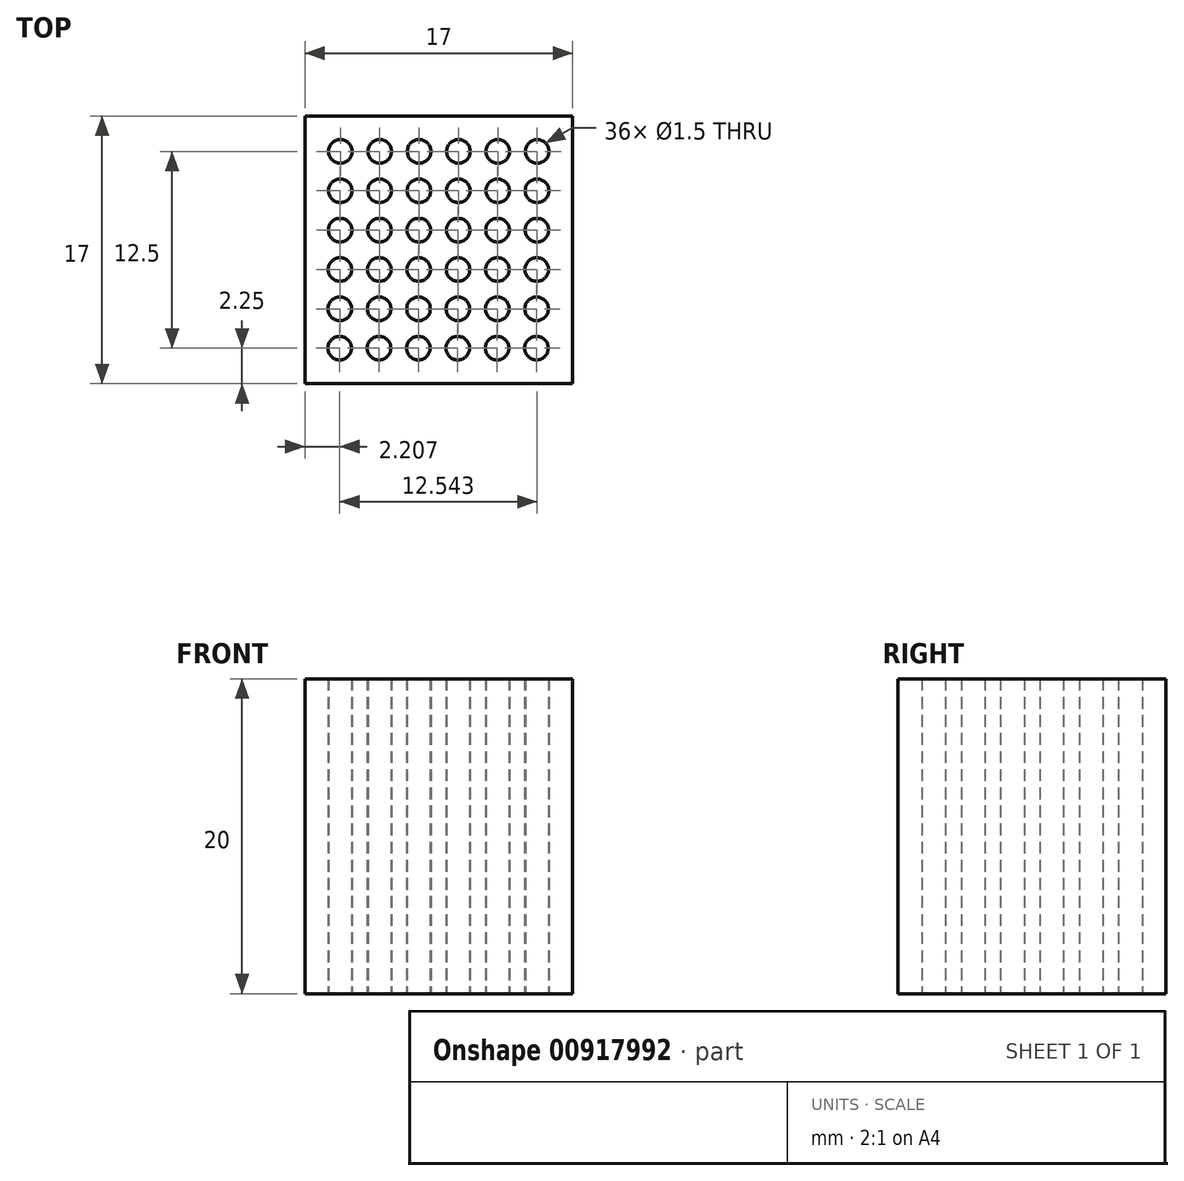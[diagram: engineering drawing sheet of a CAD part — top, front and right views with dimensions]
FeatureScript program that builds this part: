
annotation { "Feature Type Name" : "Feature", "Feature Type Description" : "" }
export const myFeature = defineFeature(function(context is Context, id is Id, definition is map)
    precondition{}
    {
        {
            var Q0;
            Q0=qCreatedBy(makeId("Top.planeOp"),FACE);
            var sketch = newSketch(context, id + "F0", { "sketchPlane" : qUnion([Q0])});
            skLineSegment(sketch, "E0.bottom", {"start": v(-8.5, 8.5) * mm, "end": v(8.5, 8.5) * mm});
            skLineSegment(sketch, "E0.top", {"start": v(-8.5, -8.5) * mm, "end": v(8.5, -8.5) * mm});
            skLineSegment(sketch, "E0.left", {"start": v(-8.5, 8.5) * mm, "end": v(-8.5, -8.5) * mm});
            skLineSegment(sketch, "E0.right", {"start": v(8.5, 8.5) * mm, "end": v(8.5, -8.5) * mm});
            skPoint(sketch, "E0.middle", {"position": v(0, 0) * mm});
            skLineSegment(sketch, "E1", {"start": v(-8.5, 8.5) * mm, "end": v(-6.25, 8.5) * mm});
            skLineSegment(sketch, "E2", {"start": v(-6.25, 8.5) * mm, "end": v(-3.75, 8.5) * mm});
            skLineSegment(sketch, "E3", {"start": v(-3.75, 8.5) * mm, "end": v(-1.25, 8.5) * mm});
            skLineSegment(sketch, "E4", {"start": v(-1.25, 8.5) * mm, "end": v(1.25, 8.5) * mm});
            skLineSegment(sketch, "E5", {"start": v(1.25, 8.5) * mm, "end": v(3.75, 8.5) * mm});
            skLineSegment(sketch, "E6", {"start": v(3.75, 8.5) * mm, "end": v(6.25, 8.5) * mm});
            skLineSegment(sketch, "E7", {"start": v(6.25, 8.5) * mm, "end": v(8.5, 8.5) * mm});
            skLineSegment(sketch, "E8", {"start": v(-8.5, 8.5) * mm, "end": v(-8.5, 6.25) * mm});
            skLineSegment(sketch, "E9", {"start": v(-8.5, 6.25) * mm, "end": v(-8.5, 3.75) * mm});
            skLineSegment(sketch, "E10", {"start": v(-8.5, 1.25) * mm, "end": v(-8.5, -1.25) * mm});
            skLineSegment(sketch, "E11", {"start": v(-8.5, -1.25) * mm, "end": v(-8.5, -3.75) * mm});
            skLineSegment(sketch, "E12", {"start": v(-8.5, -3.75) * mm, "end": v(-8.5, -6.25) * mm});
            skLineSegment(sketch, "E13", {"start": v(-8.5, -6.25) * mm, "end": v(-8.5, -8.5) * mm});
            skLineSegment(sketch, "E14", {"start": v(-8.5, 3.75) * mm, "end": v(-8.5, 1.25) * mm});
            skCircle(sketch, "E15", {"center": v(-6.25, 6.25) * mm, "radius": 0.75 * mm});
            skCircle(sketch, "E16", {"center": v(-3.75, 6.25) * mm, "radius": 0.75 * mm});
            skCircle(sketch, "E17", {"center": v(-1.25, 6.25) * mm, "radius": 0.75 * mm});
            skCircle(sketch, "E18", {"center": v(1.25, 6.25) * mm, "radius": 0.75 * mm});
            skCircle(sketch, "E19", {"center": v(3.75, 6.25) * mm, "radius": 0.75 * mm});
            skCircle(sketch, "E20", {"center": v(6.25, 6.25) * mm, "radius": 0.75 * mm});
            skCircle(sketch, "E21.1.0.0", {"center": v(-6.26, 3.75) * mm, "radius": 0.75 * mm});
            skCircle(sketch, "E21.1.0.1", {"center": v(-3.76, 3.75) * mm, "radius": 0.75 * mm});
            skCircle(sketch, "E21.1.0.2", {"center": v(-1.26, 3.75) * mm, "radius": 0.75 * mm});
            skCircle(sketch, "E21.1.0.3", {"center": v(1.24, 3.75) * mm, "radius": 0.75 * mm});
            skCircle(sketch, "E21.1.0.4", {"center": v(3.74, 3.75) * mm, "radius": 0.75 * mm});
            skCircle(sketch, "E21.1.0.5", {"center": v(6.24, 3.75) * mm, "radius": 0.75 * mm});
            skCircle(sketch, "E21.2.0.0", {"center": v(-6.27, 1.25) * mm, "radius": 0.75 * mm});
            skCircle(sketch, "E21.2.0.1", {"center": v(-3.77, 1.25) * mm, "radius": 0.75 * mm});
            skCircle(sketch, "E21.2.0.2", {"center": v(-1.27, 1.25) * mm, "radius": 0.75 * mm});
            skCircle(sketch, "E21.2.0.3", {"center": v(1.23, 1.25) * mm, "radius": 0.75 * mm});
            skCircle(sketch, "E21.2.0.4", {"center": v(3.73, 1.25) * mm, "radius": 0.75 * mm});
            skCircle(sketch, "E21.2.0.5", {"center": v(6.23, 1.25) * mm, "radius": 0.75 * mm});
            skCircle(sketch, "E21.3.0.0", {"center": v(-6.28, -1.25) * mm, "radius": 0.75 * mm});
            skCircle(sketch, "E21.3.0.1", {"center": v(-3.78, -1.25) * mm, "radius": 0.75 * mm});
            skCircle(sketch, "E21.3.0.2", {"center": v(-1.28, -1.25) * mm, "radius": 0.75 * mm});
            skCircle(sketch, "E21.3.0.3", {"center": v(1.22, -1.25) * mm, "radius": 0.75 * mm});
            skCircle(sketch, "E21.3.0.4", {"center": v(3.72, -1.25) * mm, "radius": 0.75 * mm});
            skCircle(sketch, "E21.3.0.5", {"center": v(6.22, -1.25) * mm, "radius": 0.75 * mm});
            skCircle(sketch, "E21.4.0.0", {"center": v(-6.28, -3.75) * mm, "radius": 0.75 * mm});
            skCircle(sketch, "E21.4.0.1", {"center": v(-3.78, -3.75) * mm, "radius": 0.75 * mm});
            skCircle(sketch, "E21.4.0.2", {"center": v(-1.28, -3.75) * mm, "radius": 0.75 * mm});
            skCircle(sketch, "E21.4.0.3", {"center": v(1.22, -3.75) * mm, "radius": 0.75 * mm});
            skCircle(sketch, "E21.4.0.4", {"center": v(3.72, -3.75) * mm, "radius": 0.75 * mm});
            skCircle(sketch, "E21.4.0.5", {"center": v(6.22, -3.75) * mm, "radius": 0.75 * mm});
            skCircle(sketch, "E21.5.0.0", {"center": v(-6.3, -6.25) * mm, "radius": 0.75 * mm});
            skCircle(sketch, "E21.5.0.1", {"center": v(-3.8, -6.25) * mm, "radius": 0.75 * mm});
            skCircle(sketch, "E21.5.0.2", {"center": v(-1.3, -6.25) * mm, "radius": 0.75 * mm});
            skCircle(sketch, "E21.5.0.3", {"center": v(1.2, -6.25) * mm, "radius": 0.75 * mm});
            skCircle(sketch, "E21.5.0.4", {"center": v(3.7, -6.25) * mm, "radius": 0.75 * mm});
            skCircle(sketch, "E21.5.0.5", {"center": v(6.2, -6.25) * mm, "radius": 0.75 * mm});
            skLineSegment(sketch, "E21.direction1", {"start": v(-6.25, 6.25) * mm, "end": v(-6.26, 3.75) * mm, "construction": true});
            skSolve(sketch);
        }
        {
            var Q0;
            Q0 = qSketchRegion(id + "F0", true);
            extrude(context, id + "F1", {"entities" : qUnion([Q0]), "depth" : 20 * mm, "offsetDistance" : 25 * mm});
        }
    });
